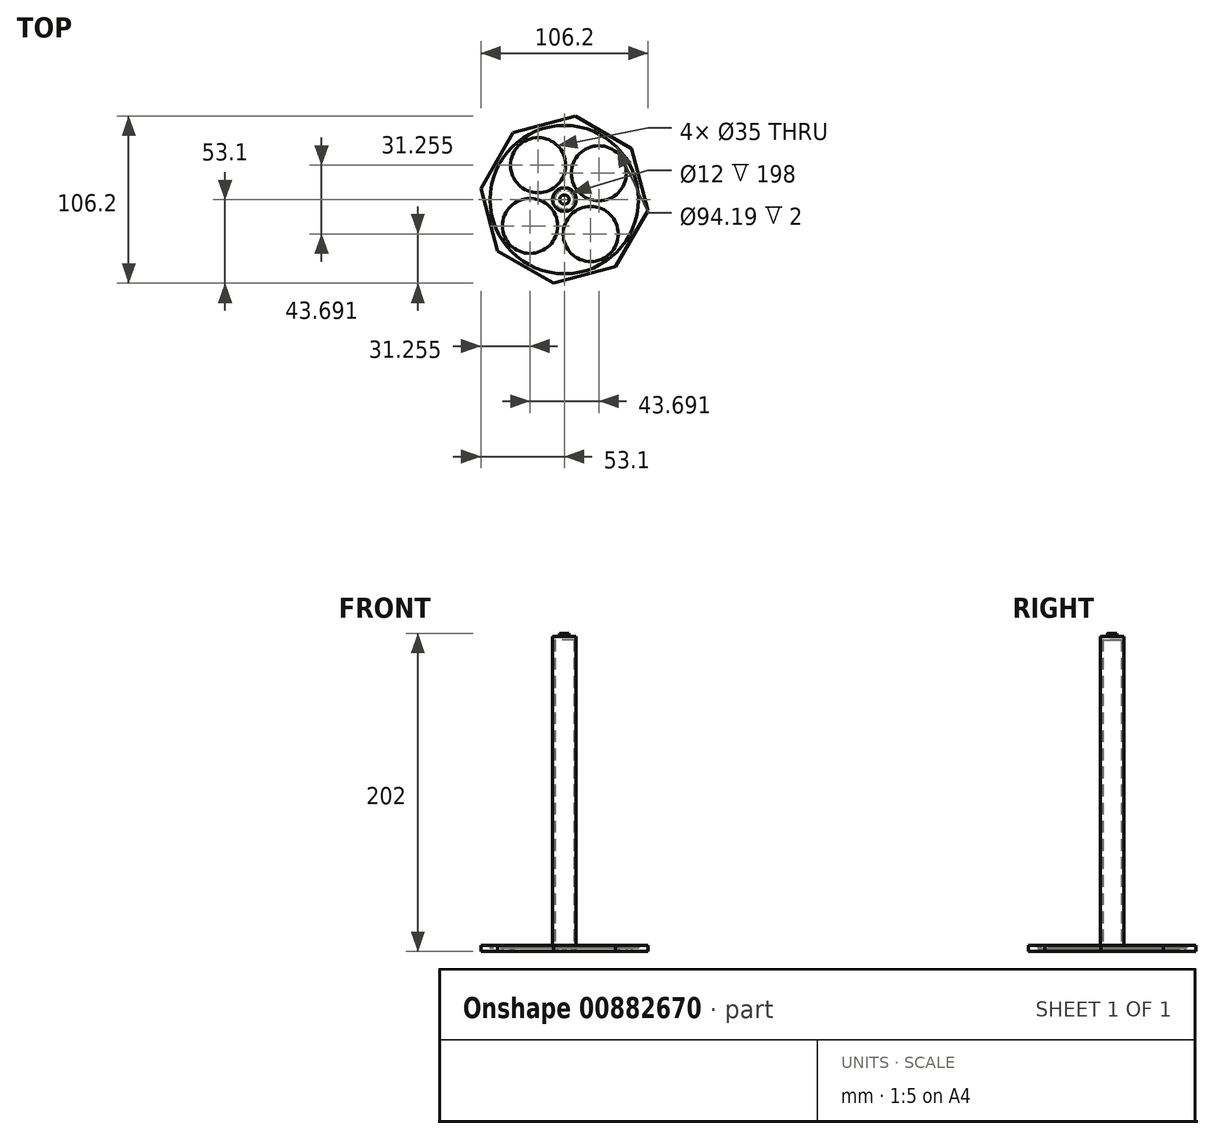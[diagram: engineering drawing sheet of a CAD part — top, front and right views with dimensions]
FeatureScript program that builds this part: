
annotation { "Feature Type Name" : "Feature", "Feature Type Description" : "" }
export const myFeature = defineFeature(function(context is Context, id is Id, definition is map)
    precondition{}
    {
        {
            var Q0;
            Q0=qCreatedBy(makeId("Top.planeOp"),FACE);
            var sketch = newSketch(context, id + "F0", { "sketchPlane" : qUnion([Q0])});
            skCircle(sketch, "E0.cCircle", {"center": v(0, 0) * mm, "radius": 49.5 * mm, "construction": true});
            skLineSegment(sketch, "E0.0", {"start": v(-53.1, 7.08) * mm, "end": v(-32.54, 42.55) * mm});
            skLineSegment(sketch, "E0.1", {"start": v(-32.54, 42.55) * mm, "end": v(7.08, 53.1) * mm});
            skLineSegment(sketch, "E0.2", {"start": v(7.08, 53.1) * mm, "end": v(42.55, 32.54) * mm});
            skLineSegment(sketch, "E0.3", {"start": v(42.55, 32.54) * mm, "end": v(53.1, -7.08) * mm});
            skLineSegment(sketch, "E0.4", {"start": v(53.1, -7.08) * mm, "end": v(32.54, -42.55) * mm});
            skLineSegment(sketch, "E0.5", {"start": v(32.54, -42.55) * mm, "end": v(-7.08, -53.1) * mm});
            skLineSegment(sketch, "E0.6", {"start": v(-7.08, -53.1) * mm, "end": v(-42.55, -32.54) * mm});
            skLineSegment(sketch, "E0.7", {"start": v(-42.55, -32.54) * mm, "end": v(-53.1, 7.08) * mm});
            skPoint(sketch, "E0.0.midPoint", {"position": v(-42.82, 24.82) * mm});
            skCircle(sketch, "E1", {"center": v(0, 0) * mm, "radius": 47.1 * mm});
            skCircle(sketch, "E2", {"center": v(0, 0) * mm, "radius": 7.5 * mm});
            skLineSegment(sketch, "E3", {"start": v(-32.54, 42.55) * mm, "end": v(32.54, -42.55) * mm, "construction": true});
            skLineSegment(sketch, "E4", {"start": v(42.55, 32.54) * mm, "end": v(-42.55, -32.54) * mm, "construction": true});
            skCircle(sketch, "E5", {"center": v(0, 0) * mm, "radius": 6 * mm});
            skCircle(sketch, "E6", {"center": v(0, 0) * mm, "radius": 27.5 * mm, "construction": true});
            skCircle(sketch, "E7", {"center": v(-21.85, -16.7) * mm, "radius": 17.5 * mm});
            skCircle(sketch, "E8.1.0", {"center": v(16.7, -21.85) * mm, "radius": 17.5 * mm});
            skCircle(sketch, "E8.2.0", {"center": v(21.85, 16.7) * mm, "radius": 17.5 * mm});
            skCircle(sketch, "E8.3.0", {"center": v(-16.7, 21.85) * mm, "radius": 17.5 * mm});
            skSolve(sketch);
        }
        {
            var Q0;
            Q0=makeQuery(id+"F0.imprint","IMPRINT",FACE,{"disambiguationData":[TD([[makeQuery(id+"F0.imprint","IMPRINT",EDGE,{"derivedFrom":sQuery(id+"F0.wireOp",EDGE,"E5")}),1.0]])]});
            var Q1;
            Q1=makeQuery(id+"F0.imprint","IMPRINT",FACE,{"disambiguationData":[TD([[makeQuery(id+"F0.imprint","IMPRINT",EDGE,{"derivedFrom":sQuery(id+"F0.wireOp",EDGE,"E2")}),1.0]])]});
            extrude(context, id + "F1", {"entities" : qUnion([Q0, Q1]), "depth" : 200 * mm, "offsetDistance" : 25 * mm});
        }
        {
            var Q0;
            Q0=makeQuery(id+"F0.imprint","IMPRINT",FACE,{"disambiguationData":[TD([[makeQuery(id+"F0.imprint","IMPRINT",EDGE,{"derivedFrom":sQuery(id+"F0.wireOp",EDGE,"E5")}),1.0]])]});
            extrude(context, id + "F2", {"entities" : qUnion([Q0]), "operationType" : NewBodyOperationType.REMOVE, "depth" : 198 * mm, "offsetDistance" : 25 * mm});
        }
        {
            var Q0;
            Q0=makeQuery(id+"F0.imprint","IMPRINT",FACE,{"disambiguationData":[TD([[makeQuery(id+"F0.imprint","IMPRINT",EDGE,{"derivedFrom":sQuery(id+"F0.wireOp",EDGE,"E1")}),1.0]])]});
            var Q1;
            Q1=makeQuery(id+"F0.imprint","IMPRINT",FACE,{"disambiguationData":[TD([[makeQuery(id+"F0.imprint","IMPRINT",EDGE,{"derivedFrom":sQuery(id+"F0.wireOp",EDGE,"E0.0")}),-1.0]])]});
            extrude(context, id + "F3", {"entities" : qUnion([Q0, Q1]), "operationType" : NewBodyOperationType.ADD, "depth" : 2 * mm, "offsetDistance" : 25 * mm});
        }
        {
            var Q0;
            Q0=makeQuery(id+"F0.imprint","IMPRINT",FACE,{"disambiguationData":[TD([[makeQuery(id+"F0.imprint","IMPRINT",EDGE,{"derivedFrom":sQuery(id+"F0.wireOp",EDGE,"E0.0")}),-1.0]])]});
            extrude(context, id + "F4", {"entities" : qUnion([Q0]), "operationType" : NewBodyOperationType.ADD, "depth" : 4 * mm, "offsetDistance" : 25 * mm});
        }
        {
            var Q0;
            Q0=makeQuery(id+"F1.opExtrude","CAP_FACE",FACE,{"disambiguationData":[OSD([sQuery(id+"F0.wireOp",EDGE,"E2")])],"isStart":false});
            cPlane(context, id + "F5", {"entities" : qUnion([Q0]), "cplaneType" : CPlaneType.OFFSET, "offset" : 0 * mm, "width" : 150 * mm, "height" : 150 * mm});
        }
        {
            var Q0;
            Q0=qCreatedBy(id+"F5.planeOp",FACE);
            var sketch = newSketch(context, id + "F6", { "sketchPlane" : qUnion([Q0])});
            skCircle(sketch, "E9", {"center": v(0, 0) * mm, "radius": 3 * mm});
            skSolve(sketch);
        }
        {
            var Q0;
            Q0=makeQuery(id+"F6.imprint","IMPRINT",FACE,{"disambiguationData":[TD([[makeQuery(id+"F6.imprint","IMPRINT",EDGE,{"derivedFrom":sQuery(id+"F6.wireOp",EDGE,"E9")}),1.0]])]});
            extrude(context, id + "F7", {"entities" : qUnion([Q0]), "operationType" : NewBodyOperationType.ADD, "depth" : 2 * mm, "offsetDistance" : 25 * mm});
        }
    });
